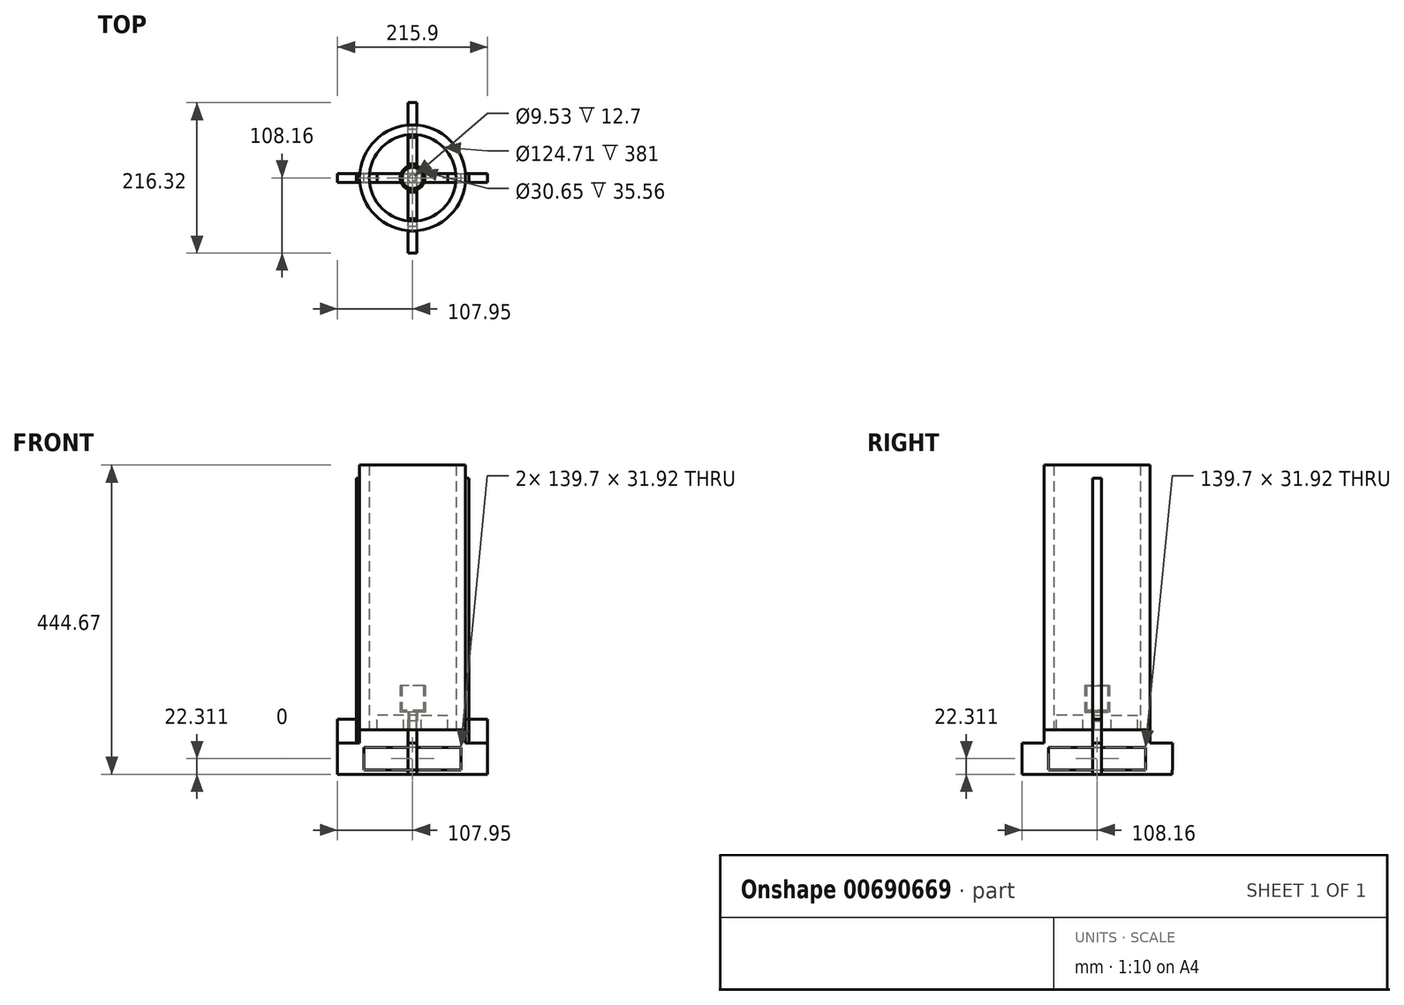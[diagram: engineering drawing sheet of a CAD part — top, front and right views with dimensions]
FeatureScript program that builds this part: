
annotation { "Feature Type Name" : "Feature", "Feature Type Description" : "" }
export const myFeature = defineFeature(function(context is Context, id is Id, definition is map)
    precondition{}
    {
        {
            var Q0;
            Q0=qCreatedBy(makeId("Top.planeOp"),FACE);
            var sketch = newSketch(context, id + "F0", { "sketchPlane" : qUnion([Q0])});
            skCircle(sketch, "E0", {"center": v(0, 0) * mm, "radius": 76.2 * mm});
            skCircle(sketch, "E1.0", {"center": v(0, 0) * mm, "radius": 62.36 * mm});
            skSolve(sketch);
        }
        {
            var Q0;
            Q0=qSketchRegion(id+"F0",true);
            extrude(context, id + "F1", {"entities" : qUnion([Q0]), "depth" : 381 * mm, "offsetDistance" : 25.4 * mm});
        }
        {
            var Q0;
            Q0=qCreatedBy(makeId("Front.planeOp"),FACE);
            var sketch = newSketch(context, id + "F2", { "sketchPlane" : qUnion([Q0])});
            skLineSegment(sketch, "E2", {"start": v(0, 0) * mm, "end": v(76.2, 0) * mm});
            skLineSegment(sketch, "E3", {"start": v(69.85, -57.32) * mm, "end": v(69.85, -25.4) * mm});
            skLineSegment(sketch, "E4", {"start": v(69.85, -25.4) * mm, "end": v(0, -25.4) * mm});
            skLineSegment(sketch, "E5", {"start": v(76.2, 0) * mm, "end": v(76.2, -19.05) * mm});
            skLineSegment(sketch, "E6", {"start": v(76.2, -19.05) * mm, "end": v(107.95, -19.05) * mm});
            skLineSegment(sketch, "E7", {"start": v(107.95, -19.05) * mm, "end": v(107.95, -57.32) * mm});
            skLineSegment(sketch, "E8", {"start": v(0, 0) * mm, "end": v(0, -25.4) * mm});
            skLineSegment(sketch, "E9", {"start": v(107.95, -57.32) * mm, "end": v(69.85, -57.32) * mm});
            skLineSegment(sketch, "E10.bottom", {"start": v(0, -57.32) * mm, "end": v(0, -57.32) * mm});
            skLineSegment(sketch, "E10.left", {"start": v(0, -57.32) * mm, "end": v(0, -63.67) * mm});
            skLineSegment(sketch, "E10.right", {"start": v(0, -57.32) * mm, "end": v(0, -63.67) * mm});
            skLineSegment(sketch, "E11.bottom", {"start": v(0, -57.32) * mm, "end": v(107.95, -57.32) * mm});
            skLineSegment(sketch, "E11.top", {"start": v(0, -63.67) * mm, "end": v(107.95, -63.67) * mm});
            skLineSegment(sketch, "E11.right", {"start": v(107.95, -57.32) * mm, "end": v(107.95, -63.67) * mm});
            skLineSegment(sketch, "E12.MirrorCS", {"start": v(-76.2, -19.05) * mm, "end": v(-107.95, -19.05) * mm});
            skLineSegment(sketch, "E13.MirrorCS", {"start": v(-76.2, 0) * mm, "end": v(-76.2, -19.05) * mm});
            skLineSegment(sketch, "E14.MirrorCS", {"start": v(-107.95, -57.32) * mm, "end": v(-69.85, -57.32) * mm});
            skLineSegment(sketch, "E15.MirrorCS", {"start": v(-107.95, -57.32) * mm, "end": v(-107.95, -63.67) * mm});
            skLineSegment(sketch, "E16.MirrorCS", {"start": v(-69.85, -25.4) * mm, "end": v(0, -25.4) * mm});
            skLineSegment(sketch, "E17.MirrorCS", {"start": v(0, -57.32) * mm, "end": v(-107.95, -57.32) * mm});
            skLineSegment(sketch, "E18.MirrorCS", {"start": v(0, -63.67) * mm, "end": v(-107.95, -63.67) * mm});
            skLineSegment(sketch, "E19.MirrorCS", {"start": v(-69.85, -57.32) * mm, "end": v(-69.85, -25.4) * mm});
            skLineSegment(sketch, "E20.MirrorCS", {"start": v(0, 0) * mm, "end": v(-76.2, 0) * mm});
            skLineSegment(sketch, "E21.MirrorCS", {"start": v(-107.95, -19.05) * mm, "end": v(-107.95, -57.32) * mm});
            skLineSegment(sketch, "E22.bottom", {"start": v(12.7, 0) * mm, "end": v(50.8, 0) * mm});
            skLineSegment(sketch, "E22.top", {"start": v(12.7, 21.11) * mm, "end": v(50.8, 21.11) * mm});
            skLineSegment(sketch, "E22.left", {"start": v(12.7, 0) * mm, "end": v(12.7, 21.11) * mm});
            skLineSegment(sketch, "E22.right", {"start": v(50.8, 0) * mm, "end": v(50.8, 21.11) * mm});
            skLineSegment(sketch, "E23.MirrorCS", {"start": v(-12.7, 0) * mm, "end": v(-12.7, 21.11) * mm});
            skLineSegment(sketch, "E24.MirrorCS", {"start": v(-12.7, 21.11) * mm, "end": v(-50.8, 21.11) * mm});
            skLineSegment(sketch, "E25.MirrorCS", {"start": v(-50.8, 0) * mm, "end": v(-50.8, 21.11) * mm});
            skSolve(sketch);
        }
        {
            var Q0;
            Q0=qSketchRegion(id+"F2",true);
            extrude(context, id + "F3", {"entities" : qUnion([Q0]), "endBound" : BoundingType.SYMMETRIC, "depth" : 12.7 * mm, "offsetDistance" : 25.4 * mm});
        }
        {
            var Q0;
            Q0=makeQuery(id+"F3.opExtrude","SWEPT_BODY",BODY,{"disambiguationData":[OSD([sQuery(id+"F2.wireOp",EDGE,"E2"),sQuery(id+"F2.wireOp",EDGE,"E3"),sQuery(id+"F2.wireOp",EDGE,"E4"),sQuery(id+"F2.wireOp",EDGE,"E5"),sQuery(id+"F2.wireOp",EDGE,"E6"),sQuery(id+"F2.wireOp",EDGE,"E7"),sQuery(id+"F2.wireOp",EDGE,"yYa1QQtk-rfeQ-uA0k-yN95-LENgFDuBBmhA"),sQuery(id+"F2.wireOp",EDGE,"RaL1Y38n-DL0R-HpUy-0Yu0-hKOuieMtGCDP"),sQuery(id+"F2.wireOp",EDGE,"KzeCX9vK-PA9l-fBDc-L8z4-hnWVkcK37siH"),sQuery(id+"F2.wireOp",EDGE,"7a3115bd-42c9-43fa-886f-b7d7f014f3800.MirrorCS"),sQuery(id+"F2.wireOp",EDGE,"93714e8b-1b55-43fa-9f0a-1818bfe9d4330.MirrorCS"),sQuery(id+"F2.wireOp",EDGE,"f685ec73-5cd7-40c9-a0cc-09a82770efb00.MirrorCS"),sQuery(id+"F2.wireOp",EDGE,"605de593-ab4b-4a38-8b95-8d2e6ad95e7e0.MirrorCS"),sQuery(id+"F2.wireOp",EDGE,"bd68596d-ea5b-43b6-8ec0-eaa4091035650.MirrorCS"),sQuery(id+"F2.wireOp",EDGE,"6dadb6d6-938b-41b2-89eb-21b29489f2620.MirrorCS"),sQuery(id+"F2.wireOp",EDGE,"35a6b2d6-89f1-42be-bee9-e52b24f0a85c0.MirrorCS"),sQuery(id+"F2.wireOp",EDGE,"99d46e2b-beb4-45a8-a67b-b38dd53197940.MirrorCS"),sQuery(id+"F2.wireOp",EDGE,"687b68df-4fec-4741-9a90-ace4315f9af80.MirrorCS")])]});
            transform(context, id + "F4", {"entities" : qUnion([Q0]), "transformType" : TransformType.COPY});
        }
        {
            var Q0;
            Q0=makeQuery(id+"F3.opExtrude","CAP_FACE",FACE,{"disambiguationData":[OSD([sQuery(id+"F2.wireOp",EDGE,"E2"),sQuery(id+"F2.wireOp",EDGE,"E3"),sQuery(id+"F2.wireOp",EDGE,"E4"),sQuery(id+"F2.wireOp",EDGE,"E5"),sQuery(id+"F2.wireOp",EDGE,"E6"),sQuery(id+"F2.wireOp",EDGE,"E7"),sQuery(id+"F2.wireOp",EDGE,"E11.bottom"),sQuery(id+"F2.wireOp",EDGE,"E11.top"),sQuery(id+"F2.wireOp",EDGE,"E11.right"),sQuery(id+"F2.wireOp",EDGE,"E12.MirrorCS"),sQuery(id+"F2.wireOp",EDGE,"E13.MirrorCS"),sQuery(id+"F2.wireOp",EDGE,"E15.MirrorCS"),sQuery(id+"F2.wireOp",EDGE,"E16.MirrorCS"),sQuery(id+"F2.wireOp",EDGE,"E17.MirrorCS"),sQuery(id+"F2.wireOp",EDGE,"E18.MirrorCS"),sQuery(id+"F2.wireOp",EDGE,"E19.MirrorCS"),sQuery(id+"F2.wireOp",EDGE,"E20.MirrorCS"),sQuery(id+"F2.wireOp",EDGE,"E21.MirrorCS")])],"isStart":false});
            var sketch = newSketch(context, id + "F5", { "sketchPlane" : qUnion([Q0])});
            skLineSegment(sketch, "E26.bottom", {"start": v(76.2, -19.05) * mm, "end": v(107.95, -19.05) * mm});
            skLineSegment(sketch, "E26.top", {"start": v(76.2, 15.16) * mm, "end": v(107.95, 15.16) * mm});
            skLineSegment(sketch, "E26.left", {"start": v(76.2, -19.05) * mm, "end": v(76.2, 15.16) * mm});
            skLineSegment(sketch, "E26.right", {"start": v(107.95, -19.05) * mm, "end": v(107.95, 15.16) * mm});
            skSolve(sketch);
        }
        {
            var Q0;
            Q0=qSketchRegion(id+"F5",true);
            extrude(context, id + "F6", {"entities" : qUnion([Q0]), "oppositeDirection" : true, "depth" : 12.7 * mm, "offsetDistance" : 25.4 * mm});
        }
        {
            var Q0;
            Q0=makeQuery(id+"F6.opExtrude","SWEPT_BODY",BODY,{"disambiguationData":[OSD([sQuery(id+"F5.wireOp",EDGE,"E26.bottom"),sQuery(id+"F5.wireOp",EDGE,"E26.top"),sQuery(id+"F5.wireOp",EDGE,"E26.left"),sQuery(id+"F5.wireOp",EDGE,"E26.right")])]});
            var Q1;
            Q1=sQuery(id+"F2.wireOp",EDGE,"E8");
            circularPattern(context, id + "F7", {"entities" : qUnion([Q0]), "axis" : qUnion([Q1]), "angle" : 360 * degree, "instanceCount" : 2, "equalSpace" : true});
        }
        {
            var Q0;
            Q0=qCreatedBy(makeId("Right.planeOp"),FACE);
            cPlane(context, id + "F8", {"entities" : qUnion([Q0]), "cplaneType" : CPlaneType.OFFSET, "offset" : 0 * mm, "oppositeDirection" : true, "width" : 152.4 * mm, "height" : 152.4 * mm});
        }
        {
            var Q0;
            Q0=qCreatedBy(id+"F8.planeOp",FACE);
            var sketch = newSketch(context, id + "F9", { "sketchPlane" : qUnion([Q0])});
            skLineSegment(sketch, "E27.bottom", {"start": v(-109.95, 11.2) * mm, "end": v(-109.95, 11.2) * mm});
            skLineSegment(sketch, "E28.0", {"start": v(0, 0) * mm, "end": v(0, -25.4) * mm});
            skLineSegment(sketch, "E29", {"start": v(0, 0) * mm, "end": v(76.2, 0) * mm});
            skLineSegment(sketch, "E30", {"start": v(69.85, -57.32) * mm, "end": v(69.85, -25.4) * mm});
            skLineSegment(sketch, "E31", {"start": v(69.85, -25.4) * mm, "end": v(0, -25.4) * mm});
            skLineSegment(sketch, "E32", {"start": v(76.2, 0) * mm, "end": v(76.2, -19.05) * mm});
            skLineSegment(sketch, "E33", {"start": v(108.16, -57.32) * mm, "end": v(69.85, -57.32) * mm});
            skLineSegment(sketch, "E34.bottom", {"start": v(5.11, -2.13) * mm, "end": v(5.11, -2.13) * mm});
            skLineSegment(sketch, "E35.bottom", {"start": v(5.27, -57.32) * mm, "end": v(107.95, -57.32) * mm});
            skLineSegment(sketch, "E35.top", {"start": v(-1.08, -63.67) * mm, "end": v(107.95, -63.67) * mm});
            skLineSegment(sketch, "E35.right", {"start": v(107.95, -57.32) * mm, "end": v(107.95, -63.67) * mm});
            skLineSegment(sketch, "E36.MirrorCS", {"start": v(-76.2, 0) * mm, "end": v(-76.2, -19.05) * mm});
            skLineSegment(sketch, "E37.MirrorCS", {"start": v(-108.16, -57.32) * mm, "end": v(-69.85, -57.32) * mm});
            skLineSegment(sketch, "E38.MirrorCS", {"start": v(-107.95, -57.32) * mm, "end": v(-107.95, -63.67) * mm});
            skLineSegment(sketch, "E39.MirrorCS", {"start": v(-69.85, -25.4) * mm, "end": v(0, -25.4) * mm});
            skLineSegment(sketch, "E40.MirrorCS", {"start": v(-5.27, -57.32) * mm, "end": v(-107.95, -57.32) * mm});
            skLineSegment(sketch, "E41.MirrorCS", {"start": v(1.08, -63.67) * mm, "end": v(-107.95, -63.67) * mm});
            skLineSegment(sketch, "E42.MirrorCS", {"start": v(-69.85, -57.32) * mm, "end": v(-69.85, -25.4) * mm});
            skLineSegment(sketch, "E43.MirrorCS", {"start": v(0, 0) * mm, "end": v(-76.2, 0) * mm});
            skLineSegment(sketch, "E44.bottom", {"start": v(-20.32, 0) * mm, "end": v(-58.42, 0) * mm});
            skLineSegment(sketch, "E44.top", {"start": v(-20.32, 21.11) * mm, "end": v(-58.42, 21.11) * mm});
            skLineSegment(sketch, "E44.left", {"start": v(-20.32, 0) * mm, "end": v(-20.32, 21.11) * mm});
            skLineSegment(sketch, "E44.right", {"start": v(-58.42, 0) * mm, "end": v(-58.42, 21.11) * mm});
            skPoint(sketch, "E45.0", {"position": v(0, 21.11) * mm});
            skLineSegment(sketch, "E46", {"start": v(0, 21.11) * mm, "end": v(-20.32, 21.11) * mm, "construction": true});
            skLineSegment(sketch, "E47.MirrorCS", {"start": v(20.32, 0) * mm, "end": v(20.32, 21.11) * mm});
            skLineSegment(sketch, "E48.MirrorCS", {"start": v(20.32, 21.11) * mm, "end": v(58.42, 21.11) * mm});
            skLineSegment(sketch, "E49.MirrorCS", {"start": v(58.42, 0) * mm, "end": v(58.42, 21.11) * mm});
            skLineSegment(sketch, "E50", {"start": v(-76.2, -19.05) * mm, "end": v(-108.16, -19.05) * mm});
            skLineSegment(sketch, "E51", {"start": v(-108.16, -19.05) * mm, "end": v(-108.16, -57.32) * mm});
            skLineSegment(sketch, "E52.MirrorCS", {"start": v(76.2, -19.05) * mm, "end": v(108.16, -19.05) * mm});
            skLineSegment(sketch, "E53.MirrorCS", {"start": v(108.16, -19.05) * mm, "end": v(108.16, -57.32) * mm});
            skLineSegment(sketch, "E54", {"start": v(-5.27, -57.32) * mm, "end": v(5.27, -57.32) * mm});
            skSolve(sketch);
        }
        {
            var Q0;
            Q0=qSketchRegion(id+"F9",true);
            extrude(context, id + "F10", {"entities" : qUnion([Q0]), "endBound" : BoundingType.SYMMETRIC, "depth" : 12.7 * mm, "offsetDistance" : 25.4 * mm});
        }
        {
            var Q0;
            Q0=qCreatedBy(makeId("Top.planeOp"),FACE);
            var sketch = newSketch(context, id + "F11", { "sketchPlane" : qUnion([Q0])});
            skPoint(sketch, "E55.0", {"position": v(0, 0) * mm});
            skCircle(sketch, "E56", {"center": v(0, 0) * mm, "radius": 4.76 * mm});
            skSolve(sketch);
        }
        {
            var Q0;
            Q0=qSketchRegion(id+"F11",true);
            extrude(context, id + "F12", {"entities" : qUnion([Q0]), "depth" : 12.7 * mm, "offsetDistance" : 25.4 * mm});
        }
        {
            var Q0;
            Q0=makeQuery(id+"F12.opExtrude","CAP_FACE",FACE,{"disambiguationData":[OSD([sQuery(id+"F11.wireOp",EDGE,"E56")])],"isStart":false});
            var sketch = newSketch(context, id + "F13", { "sketchPlane" : qUnion([Q0])});
            skCircle(sketch, "E57.0.0", {"center": v(0, 0) * mm, "radius": 4.76 * mm});
            skCircle(sketch, "E58", {"center": v(0, 0) * mm, "radius": 6.61 * mm});
            skSolve(sketch);
        }
        {
            var Q0;
            Q0=qSketchRegion(id+"F13",true);
            extrude(context, id + "F14", {"entities" : qUnion([Q0]), "depth" : 12.7 * mm, "offsetDistance" : 25.4 * mm});
        }
        {
            var Q0;
            Q0=makeQuery(id+"F14.opExtrude","CAP_FACE",FACE,{"disambiguationData":[OSD([sQuery(id+"F13.wireOp",EDGE,"E57.0.0"),sQuery(id+"F13.wireOp",EDGE,"E58")])],"isStart":false});
            var sketch = newSketch(context, id + "F15", { "sketchPlane" : qUnion([Q0])});
            skCircle(sketch, "E59", {"center": v(0, 0) * mm, "radius": 17.86 * mm});
            skSolve(sketch);
        }
        {
            var Q0;
            Q0=qSketchRegion(id+"F15",true);
            extrude(context, id + "F16", {"entities" : qUnion([Q0]), "depth" : 38.1 * mm, "offsetDistance" : 25.4 * mm});
        }
        {
            var Q0;
            Q0=makeQuery(id+"F16.opExtrude","CAP_FACE",FACE,{"disambiguationData":[OSD([sQuery(id+"F15.wireOp",EDGE,"E59")])],"isStart":false});
            shell(context, id + "F17", {"entities" : qUnion([Q0]), "thickness" : 2.54 * mm});
        }
        {
            var Q0;
            Q0=qCreatedBy(makeId("Front.planeOp"),FACE);
            var sketch = newSketch(context, id + "F18", { "sketchPlane" : qUnion([Q0])});
            skLineSegment(sketch, "E60.top", {"start": v(76.2, 361.95) * mm, "end": v(80.96, 361.95) * mm});
            skLineSegment(sketch, "E60.left", {"start": v(76.2, -19.05) * mm, "end": v(76.2, 361.95) * mm});
            skLineSegment(sketch, "E60.right", {"start": v(80.96, -19.05) * mm, "end": v(80.96, 361.95) * mm});
            skPoint(sketch, "E61.0", {"position": v(76.2, -19.05) * mm});
            skLineSegment(sketch, "E62", {"start": v(76.2, -19.05) * mm, "end": v(80.96, -19.05) * mm});
            skSolve(sketch);
        }
        {
            var Q0;
            Q0 = qSketchRegion(id + "F18", true);
            extrude(context, id + "F19", {"entities" : qUnion([Q0]), "endBound" : BoundingType.SYMMETRIC, "depth" : 12.7 * mm, "offsetDistance" : 25.4 * mm});
        }
        {
            var Q0;
            Q0=makeQuery(id+"F19.opExtrude","SWEPT_BODY",BODY,{"disambiguationData":[OSD([sQuery(id+"F18.wireOp",EDGE,"E60.top"),sQuery(id+"F18.wireOp",EDGE,"E60.left"),sQuery(id+"F18.wireOp",EDGE,"E60.right"),sQuery(id+"F18.wireOp",EDGE,"E62")])]});
            var Q1;
            Q1=sQuery(id+"F2.wireOp",EDGE,"E8");
            circularPattern(context, id + "F20", {"entities" : qUnion([Q0]), "axis" : qUnion([Q1]), "angle" : 360 * degree, "instanceCount" : 2, "equalSpace" : true});
        }
    });
